# Revit family: Hager-Volta-IP30-Hollow_wall-syst-PL-pl
name_source: partatom
category: Electrical Equipment
units: mm (PartAtom-declared; Revit-internal decimal feet)

## family parameters
Cut with Voids When Loaded = No
Host = Face
Panel Configuration = Two Columns, Circuits Across
Part Type = Panelboard
Room Calculation Point = No
Round Connector Dimension = Use Diameter
Shared = No

## types (10) — shared parameters
EF000003 - Sposób montażu = EV000128 - Do ścian pustych
EF000007 - Kolor = EV000202 - Biały
EF000008 - Szerokość = 348 mm  [stored 1.14173 ft]
EF000116 - Numer RAL = 9010
EF000118 - Z płytą montażową = No
EF000218 - Głębokość wbudowania = 89 mm  [stored 0.291995 ft]
EF000339 - Rodzaj pokrywy = EV004216 - Drzwi
EF000846 - Szerokość wbudowania = 314 mm  [stored 1.03018 ft]
EF001062 - Wykonane zgodnie z Dyrektywą Kompatybilności Elektromagnetycznej EMC = No
EF001088 - Możliwość rozbudowy = Yes
EF001131 - Głębokość wewnętrzna = 92 mm
EF001134 - Szyna DIN = Yes
EF002950 - Szerokość wyrażona liczbą modułów = 12
EF004462 - Rodzaj zamknięcia = EV000154 - Inne
EF005474 - Stopień ochrony (IP) = EV006410 - IP30
EF006244 - Transparentna pokrywa/drzwi = No
EF006306 - Z zamkiem = No
EF009212 - Wykonanie pokrywy = EV009916 - Z otworem
EF015941 - Drzwi przepuszczające sygnał = No
HG000001 - Liczba kolumn = 1
HG000002 - Z drzwiami lub pokrywą = Yes
HG000003 - Zakres = Volta
HG000005 - Grubość = 3 mm  [stored 0.00984252 ft]
HG000006 - Montaż podtynkowy = Yes
HG000009 - Drzwi dwuskrzydłowe = No
HG000010 - Drzwi asymetryczne = No
HG000011 - Puste rzędy od dołu = No
HG000017 - Odległość między biegunami = 18 mm  [stored 0.0590551 ft]
Manufacturer = Hager
Type Comments = Volta
zero-valued in all types: Default Elevation, HG000007 - Liczba pustych kolumn, HG000008 - Liczba pustych rzędów

## per-type parameters (varying)
| type | EF000040 - Wysokość | EF000049 - Głębokość | EF000266 - Liczba rzędów | EF000332 - Wysokość wbudowania | EF001596 - Materiał obudowy | EF015776 - Listwa zaciskowa uziemienia | EF015777 - Listwa zaciskowa przewodu neutralnego | HG000004 - Referencja producenta | Model |
| Montaż podtynkowy IP30 S348 W356.5 G98 12 Jednostki dywizyjne - VH12AT | 356 mm | 98 mm  [stored 0.321522 ft] | 1 | 321 mm | EV000139 - Tworzywo sztuczne | Yes | Yes | VH12AT | VH12AT |
| Montaż podtynkowy IP30 S348 W356.5 G98 12 Jednostki dywizyjne - VH12NE | 356 mm | 98 mm  [stored 0.321522 ft] | 1 | 321 mm | EV000139 - Tworzywo sztuczne | Yes | No | VH12NE | VH12NE |
| Montaż podtynkowy IP30 S348 W505.5 G98 12 Jednostki dywizyjne - VH24AT | 506 mm | 98 mm  [stored 0.321522 ft] | 2 | 470 mm | EV000139 - Tworzywo sztuczne | Yes | Yes | VH24AT | VH24AT |
| Montaż podtynkowy IP30 S348 W505.5 G98 12 Jednostki dywizyjne - VH24NE | 506 mm | 98 mm  [stored 0.321522 ft] | 2 | 470 mm | EV000139 - Tworzywo sztuczne | Yes | No | VH24NE | VH24NE |
| Montaż podtynkowy IP30 S348 W630.5 G98 12 Jednostki dywizyjne - VH36AT | 630 mm | 98 mm  [stored 0.321522 ft] | 3 | 595 mm | EV000139 - Tworzywo sztuczne | Yes | Yes | VH36AT | VH36AT |
| Montaż podtynkowy IP30 S348 W630.5 G98 12 Jednostki dywizyjne - VH36NE | 630 mm | 98 mm  [stored 0.321522 ft] | 3 | 595 mm | EV000139 - Tworzywo sztuczne | Yes | No | VH36NE | VH36NE |
| Montaż podtynkowy IP30 S348 W755.5 G98 12 Jednostki dywizyjne - VH48AT | 756 mm | 98 mm  [stored 0.321522 ft] | 4 | 720 mm  [stored 2.3622 ft] | EV000139 - Tworzywo sztuczne | Yes | Yes | VH48AT | VH48AT |
| Montaż podtynkowy IP30 S348 W755.5 G98 12 Jednostki dywizyjne - VH48NE | 756 mm | 98 mm  [stored 0.321522 ft] | 4 | 720 mm  [stored 2.3622 ft] | EV000139 - Tworzywo sztuczne | Yes | No | VH48NE | VH48NE |
| Montaż podtynkowy IP30 S348 W880.5 G94.5 12 Jednostki dywizyjne - VH60NC | 880 mm  [stored 2.88714 ft] | 94 mm | 5 | 846 mm | EV000139 - Tworzywo sztuczne | No | No | VH60NC | VH60NC |
| Montaż podtynkowy IP30 S348 W880.5 G98 12 Jednostki dywizyjne - VH60AT | 880 mm  [stored 2.88714 ft] | 98 mm  [stored 0.321522 ft] | 5 | 845 mm  [stored 2.77231 ft] | EV000154 - Inne | Yes | No | VH60AT | VH60AT |

note: [stored X ft] marks values corroborated as IEEE doubles in the binary element streams (Revit-internal decimal feet)

## geometry (parser evidence)
native form markers: Sweep x17
no freeform markers — native parametric forms only
